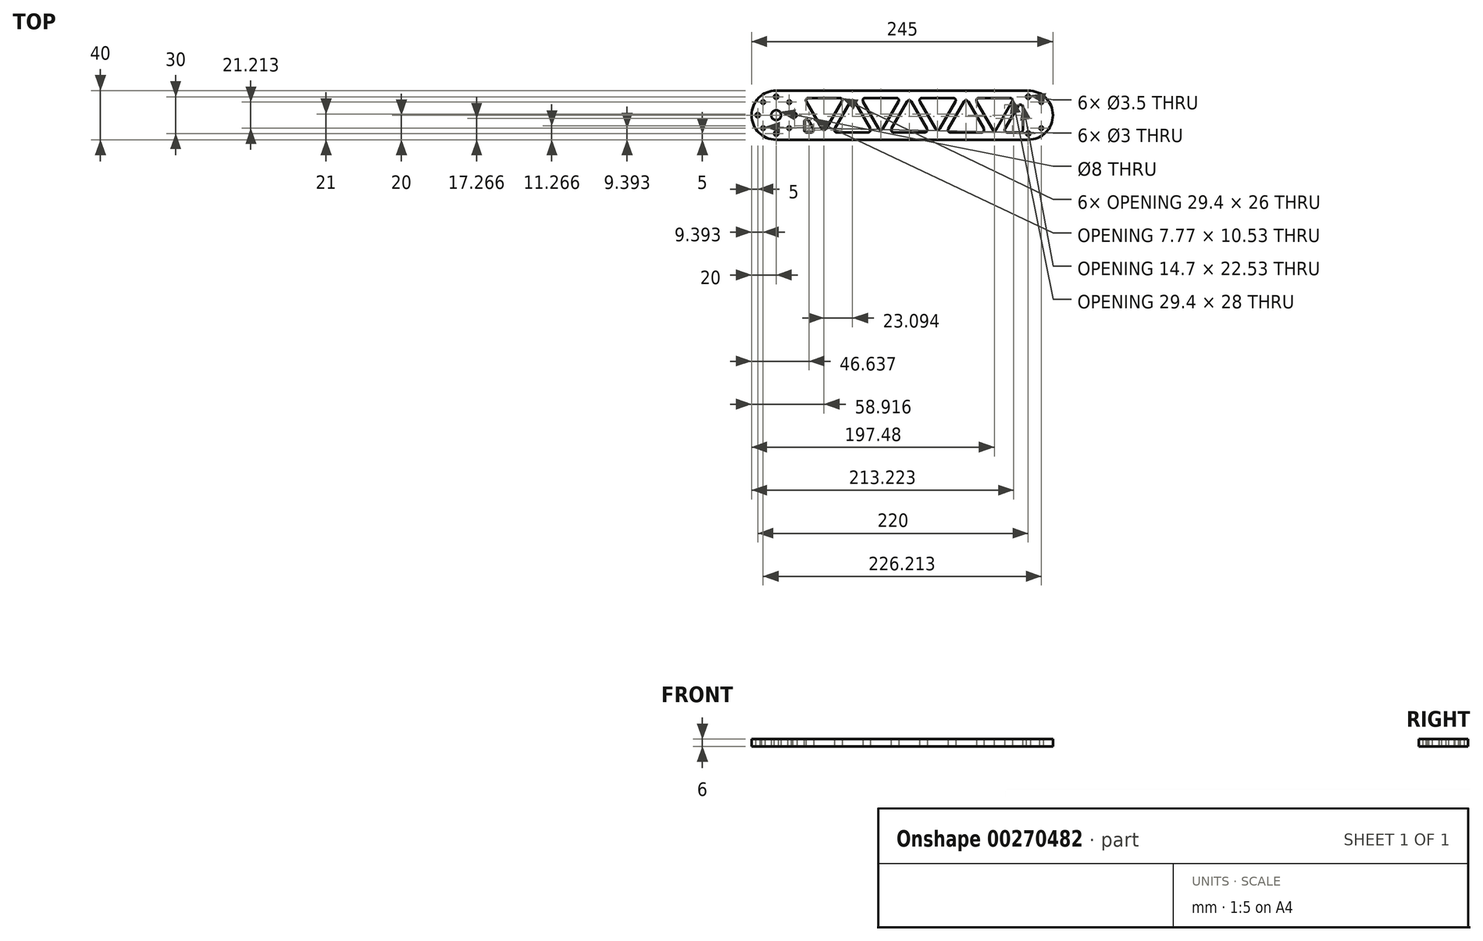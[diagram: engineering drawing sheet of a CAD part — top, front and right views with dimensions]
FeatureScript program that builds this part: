
annotation { "Feature Type Name" : "Feature", "Feature Type Description" : "" }
export const myFeature = defineFeature(function(context is Context, id is Id, definition is map)
    precondition{}
    {
        {
            var Q0;
            Q0=qCreatedBy(makeId("Top.planeOp"),FACE);
            var sketch = newSketch(context, id + "F0", { "sketchPlane" : qUnion([Q0])});
            skLineSegment(sketch, "E0.bottom", {"start": v(0, 0) * mm, "end": v(205, 0) * mm});
            skLineSegment(sketch, "E0.top", {"start": v(0, 40) * mm, "end": v(205, 40) * mm});
            skArc(sketch, "E1", {"start": v(205, 40) * mm, "mid": v(225, 20) * mm, "end": v(205, 0) * mm});
            skArc(sketch, "E2", {"start": v(0, 40) * mm, "mid": v(-20, 20) * mm, "end": v(0, 0) * mm});
            skCircle(sketch, "E3", {"center": v(0, 20) * mm, "radius": 15 * mm, "construction": true});
            skCircle(sketch, "E4", {"center": v(0, 35) * mm, "radius": 1.75 * mm});
            skCircle(sketch, "E5.1.0", {"center": v(-15, 20) * mm, "radius": 1.75 * mm});
            skCircle(sketch, "E5.2.0", {"center": v(0, 5) * mm, "radius": 1.75 * mm});
            skCircle(sketch, "E5.3.0", {"center": v(15, 20) * mm, "radius": 1.75 * mm});
            skLineSegment(sketch, "E6", {"start": v(0, 20) * mm, "end": v(10.6, 30.6) * mm});
            skCircle(sketch, "E7", {"center": v(10.6, 30.6) * mm, "radius": 1.5 * mm});
            skCircle(sketch, "E8.1.0", {"center": v(-10.6, 30.6) * mm, "radius": 1.5 * mm});
            skCircle(sketch, "E8.2.0", {"center": v(-10.6, 9.4) * mm, "radius": 1.5 * mm});
            skCircle(sketch, "E8.3.0", {"center": v(10.6, 9.4) * mm, "radius": 1.5 * mm});
            skCircle(sketch, "E9", {"center": v(0, 20) * mm, "radius": 4 * mm});
            skLineSegment(sketch, "E10", {"start": v(102.5, 40) * mm, "end": v(102.5, 0) * mm, "construction": true});
            skCircle(sketch, "E11.MirrorC", {"center": v(215.6, 30.6) * mm, "radius": 1.5 * mm});
            skCircle(sketch, "E12.MirrorC", {"center": v(215.6, 9.4) * mm, "radius": 1.5 * mm});
            skLineSegment(sketch, "E13.MirrorCS", {"start": v(205, 20) * mm, "end": v(194.4, 30.6) * mm});
            skCircle(sketch, "E14.MirrorC", {"center": v(205, 20) * mm, "radius": 15 * mm, "construction": true});
            skCircle(sketch, "E15", {"center": v(205, 5) * mm, "radius": 1.75 * mm});
            skCircle(sketch, "E16", {"center": v(205, 35) * mm, "radius": 1.75 * mm});
            skSolve(sketch);
        }
        {
            var Q0;
            Q0 = qSketchRegion(id + "F0", true);
            extrude(context, id + "F1", {"entities" : qUnion([Q0]), "depth" : 6 * mm});
        }
        {
            var Q0;
            Q0=makeQuery(id+"F1.opExtrude","CAP_FACE",FACE,{"disambiguationData":[OSD([sQuery(id+"F0.wireOp",EDGE,"E0.bottom"),sQuery(id+"F0.wireOp",EDGE,"E0.top"),sQuery(id+"F0.wireOp",EDGE,"E2"),sQuery(id+"F0.wireOp",EDGE,"E4"),sQuery(id+"F0.wireOp",EDGE,"E5.1.0"),sQuery(id+"F0.wireOp",EDGE,"E5.2.0"),sQuery(id+"F0.wireOp",EDGE,"E5.3.0"),sQuery(id+"F0.wireOp",EDGE,"E7"),sQuery(id+"F0.wireOp",EDGE,"E8.1.0"),sQuery(id+"F0.wireOp",EDGE,"E8.2.0"),sQuery(id+"F0.wireOp",EDGE,"E8.3.0"),sQuery(id+"F0.wireOp",EDGE,"E9"),sQuery(id+"F0.wireOp",EDGE,"41661442-f439-4f29-86a3-6f938a79d0c80.MirrorC"),sQuery(id+"F0.wireOp",EDGE,"E11.MirrorC"),sQuery(id+"F0.wireOp",EDGE,"E12.MirrorC"),sQuery(id+"F0.wireOp",EDGE,"E1"),sQuery(id+"F0.wireOp",EDGE,"41661442-f439-4f29-86a3-6f938a79d0c812.MirrorC")])],"isStart":false});
            var sketch = newSketch(context, id + "F2", { "sketchPlane" : qUnion([Q0])});
            skLineSegment(sketch, "E17.left", {"start": v(22.75, 34) * mm, "end": v(22.75, 6) * mm, "construction": true});
            skLineSegment(sketch, "E17.right", {"start": v(200.57, 33.96) * mm, "end": v(200.57, 6) * mm, "construction": true});
            skLineSegment(sketch, "E18", {"start": v(22.75, 34) * mm, "end": v(55.08, 34) * mm});
            skLineSegment(sketch, "E19", {"start": v(55.08, 34) * mm, "end": v(38.92, 6) * mm});
            skLineSegment(sketch, "E20", {"start": v(38.92, 6) * mm, "end": v(22.75, 34) * mm});
            skLineSegment(sketch, "E21", {"start": v(45.84, 6) * mm, "end": v(62, 34) * mm});
            skLineSegment(sketch, "E22", {"start": v(62, 34) * mm, "end": v(78.18, 6) * mm});
            skLineSegment(sketch, "E23", {"start": v(78.18, 6) * mm, "end": v(45.84, 6) * mm});
            skLineSegment(sketch, "E24", {"start": v(22.75, 6) * mm, "end": v(200.57, 6) * mm, "construction": true});
            skLineSegment(sketch, "E25", {"start": v(55.08, 34) * mm, "end": v(22.75, 34) * mm, "construction": true});
            skPoint(sketch, "E26.visualSharp", {"position": v(22.75, 34) * mm});
            skPoint(sketch, "E27.visualSharp", {"position": v(38.92, 6) * mm});
            skLineSegment(sketch, "E28.1.0.0", {"start": v(101.27, 34) * mm, "end": v(85.1, 6) * mm});
            skPoint(sketch, "E28.1.0.1", {"position": v(68.94, 34) * mm});
            skLineSegment(sketch, "E28.1.0.2", {"start": v(85.1, 6) * mm, "end": v(68.94, 34) * mm});
            skLineSegment(sketch, "E28.1.0.3", {"start": v(108.2, 34) * mm, "end": v(124.36, 6) * mm});
            skLineSegment(sketch, "E28.1.0.4", {"start": v(92.03, 6) * mm, "end": v(108.2, 34) * mm});
            skPoint(sketch, "E28.1.0.5", {"position": v(85.1, 6) * mm});
            skLineSegment(sketch, "E28.1.0.6", {"start": v(101.27, 34) * mm, "end": v(68.94, 34) * mm, "construction": true});
            skLineSegment(sketch, "E28.1.0.7", {"start": v(124.36, 6) * mm, "end": v(92.03, 6) * mm});
            skLineSegment(sketch, "E28.1.0.8", {"start": v(68.94, 34) * mm, "end": v(101.27, 34) * mm});
            skLineSegment(sketch, "E28.2.0.0", {"start": v(147.46, 34) * mm, "end": v(131.3, 6) * mm});
            skPoint(sketch, "E28.2.0.1", {"position": v(115.13, 34) * mm});
            skLineSegment(sketch, "E28.2.0.2", {"start": v(131.3, 6) * mm, "end": v(115.13, 34) * mm});
            skLineSegment(sketch, "E28.2.0.3", {"start": v(154.39, 34) * mm, "end": v(170.55, 6) * mm});
            skLineSegment(sketch, "E28.2.0.4", {"start": v(138.22, 6) * mm, "end": v(154.39, 34) * mm});
            skPoint(sketch, "E28.2.0.5", {"position": v(131.3, 6) * mm});
            skLineSegment(sketch, "E28.2.0.6", {"start": v(147.46, 34) * mm, "end": v(115.13, 34) * mm, "construction": true});
            skLineSegment(sketch, "E28.2.0.7", {"start": v(170.55, 6) * mm, "end": v(138.22, 6) * mm});
            skLineSegment(sketch, "E28.2.0.8", {"start": v(115.13, 34) * mm, "end": v(147.46, 34) * mm});
            skLineSegment(sketch, "E28.direction1", {"start": v(38.92, 6) * mm, "end": v(85.1, 6) * mm, "construction": true});
            skLineSegment(sketch, "E29.0.3.0", {"start": v(193.65, 34) * mm, "end": v(177.48, 6) * mm});
            skPoint(sketch, "E29.3.3.0", {"position": v(161.31, 34) * mm});
            skLineSegment(sketch, "E29.4.3.0", {"start": v(177.48, 6) * mm, "end": v(161.31, 34) * mm});
            skPoint(sketch, "E29.13.3.0", {"position": v(177.48, 6) * mm});
            skLineSegment(sketch, "E29.14.3.0", {"start": v(193.65, 34) * mm, "end": v(161.31, 34) * mm, "construction": true});
            skLineSegment(sketch, "E29.20.3.0", {"start": v(161.31, 34) * mm, "end": v(193.65, 34) * mm});
            skLineSegment(sketch, "E30", {"start": v(200.57, 34) * mm, "end": v(184.4, 6) * mm});
            skLineSegment(sketch, "E31", {"start": v(184.4, 6) * mm, "end": v(200.57, 6) * mm});
            skLineSegment(sketch, "E32", {"start": v(200.57, 6) * mm, "end": v(200.57, 34) * mm});
            skLineSegment(sketch, "E33", {"start": v(22.75, 6) * mm, "end": v(31.99, 6) * mm});
            skLineSegment(sketch, "E34", {"start": v(31.99, 6) * mm, "end": v(22.75, 22) * mm});
            skLineSegment(sketch, "E35", {"start": v(22.75, 22) * mm, "end": v(22.75, 6) * mm});
            skSolve(sketch);
        }
        {
            var Q0;
            Q0 = qSketchRegion(id + "F2", true);
            extrude(context, id + "F3", {"entities" : qUnion([Q0]), "operationType" : NewBodyOperationType.REMOVE, "endBound" : BoundingType.THROUGH_ALL, "oppositeDirection" : true, "depth" : 25 * mm});
        }
        {
            var Q0;
            Q0=makeQuery(id+"F3.boolean.opBoolean","COPY",EDGE,{"derivedFrom":makeQuery(id+"F3.opExtrude","SWEPT_EDGE",EDGE,{"disambiguationData":[OSD([sQuery(id+"F2.wireOp",EDGE,"E18"),sQuery(id+"F2.wireOp",EDGE,"E20")])]})});
            var Q1;
            Q1=makeQuery(id+"F3.boolean.opBoolean","COPY",EDGE,{"derivedFrom":makeQuery(id+"F3.opExtrude","SWEPT_EDGE",EDGE,{"disambiguationData":[OSD([sQuery(id+"F2.wireOp",EDGE,"E18"),sQuery(id+"F2.wireOp",EDGE,"E19")])]})});
            var Q2;
            Q2=makeQuery(id+"F3.boolean.opBoolean","COPY",EDGE,{"derivedFrom":makeQuery(id+"F3.opExtrude","SWEPT_EDGE",EDGE,{"disambiguationData":[OSD([sQuery(id+"F2.wireOp",EDGE,"E19"),sQuery(id+"F2.wireOp",EDGE,"E20")])]})});
            var Q3;
            Q3=makeQuery(id+"F3.boolean.opBoolean","COPY",EDGE,{"derivedFrom":makeQuery(id+"F3.opExtrude","SWEPT_EDGE",EDGE,{"disambiguationData":[OSD([sQuery(id+"F2.wireOp",EDGE,"E21"),sQuery(id+"F2.wireOp",EDGE,"E23")])]})});
            var Q4;
            Q4=makeQuery(id+"F3.boolean.opBoolean","COPY",EDGE,{"derivedFrom":makeQuery(id+"F3.opExtrude","SWEPT_EDGE",EDGE,{"disambiguationData":[OSD([sQuery(id+"F2.wireOp",EDGE,"E21"),sQuery(id+"F2.wireOp",EDGE,"E22")])]})});
            var Q5;
            Q5=makeQuery(id+"F3.boolean.opBoolean","COPY",EDGE,{"derivedFrom":makeQuery(id+"F3.opExtrude","SWEPT_EDGE",EDGE,{"disambiguationData":[OSD([sQuery(id+"F2.wireOp",EDGE,"E22"),sQuery(id+"F2.wireOp",EDGE,"E23")])]})});
            var Q6;
            Q6=makeQuery(id+"F3.boolean.opBoolean","COPY",EDGE,{"derivedFrom":makeQuery(id+"F3.opExtrude","SWEPT_EDGE",EDGE,{"disambiguationData":[OSD([sQuery(id+"F2.wireOp",EDGE,"E34"),sQuery(id+"F2.wireOp",EDGE,"E35")])]})});
            var Q7;
            Q7=makeQuery(id+"F3.boolean.opBoolean","COPY",EDGE,{"derivedFrom":makeQuery(id+"F3.opExtrude","SWEPT_EDGE",EDGE,{"disambiguationData":[OSD([sQuery(id+"F2.wireOp",EDGE,"E33"),sQuery(id+"F2.wireOp",EDGE,"E35")])]})});
            var Q8;
            Q8=makeQuery(id+"F3.boolean.opBoolean","COPY",EDGE,{"derivedFrom":makeQuery(id+"F3.opExtrude","SWEPT_EDGE",EDGE,{"disambiguationData":[OSD([sQuery(id+"F2.wireOp",EDGE,"E33"),sQuery(id+"F2.wireOp",EDGE,"E34")])]})});
            var Q9;
            Q9=makeQuery(id+"F3.boolean.opBoolean","COPY",EDGE,{"derivedFrom":makeQuery(id+"F3.opExtrude","SWEPT_EDGE",EDGE,{"disambiguationData":[OSD([sQuery(id+"F2.wireOp",EDGE,"E28.1.0.2"),sQuery(id+"F2.wireOp",EDGE,"E28.1.0.8")])]})});
            var Q10;
            Q10=makeQuery(id+"F3.boolean.opBoolean","COPY",EDGE,{"derivedFrom":makeQuery(id+"F3.opExtrude","SWEPT_EDGE",EDGE,{"disambiguationData":[OSD([sQuery(id+"F2.wireOp",EDGE,"E28.1.0.0"),sQuery(id+"F2.wireOp",EDGE,"E28.1.0.8")])]})});
            var Q11;
            Q11=makeQuery(id+"F3.boolean.opBoolean","COPY",EDGE,{"derivedFrom":makeQuery(id+"F3.opExtrude","SWEPT_EDGE",EDGE,{"disambiguationData":[OSD([sQuery(id+"F2.wireOp",EDGE,"E28.1.0.0"),sQuery(id+"F2.wireOp",EDGE,"E28.1.0.2")])]})});
            var Q12;
            Q12=makeQuery(id+"F3.boolean.opBoolean","COPY",EDGE,{"derivedFrom":makeQuery(id+"F3.opExtrude","SWEPT_EDGE",EDGE,{"disambiguationData":[OSD([sQuery(id+"F2.wireOp",EDGE,"E28.1.0.4"),sQuery(id+"F2.wireOp",EDGE,"E28.1.0.7")])]})});
            var Q13;
            Q13=makeQuery(id+"F3.boolean.opBoolean","COPY",EDGE,{"derivedFrom":makeQuery(id+"F3.opExtrude","SWEPT_EDGE",EDGE,{"disambiguationData":[OSD([sQuery(id+"F2.wireOp",EDGE,"E28.1.0.3"),sQuery(id+"F2.wireOp",EDGE,"E28.1.0.4")])]})});
            var Q14;
            Q14=makeQuery(id+"F3.boolean.opBoolean","COPY",EDGE,{"derivedFrom":makeQuery(id+"F3.opExtrude","SWEPT_EDGE",EDGE,{"disambiguationData":[OSD([sQuery(id+"F2.wireOp",EDGE,"E28.1.0.3"),sQuery(id+"F2.wireOp",EDGE,"E28.1.0.7")])]})});
            var Q15;
            Q15=makeQuery(id+"F3.boolean.opBoolean","COPY",EDGE,{"derivedFrom":makeQuery(id+"F3.opExtrude","SWEPT_EDGE",EDGE,{"disambiguationData":[OSD([sQuery(id+"F2.wireOp",EDGE,"E28.2.0.2"),sQuery(id+"F2.wireOp",EDGE,"E28.2.0.8")])]})});
            var Q16;
            Q16=makeQuery(id+"F3.boolean.opBoolean","COPY",EDGE,{"derivedFrom":makeQuery(id+"F3.opExtrude","SWEPT_EDGE",EDGE,{"disambiguationData":[OSD([sQuery(id+"F2.wireOp",EDGE,"E29.4.3.0"),sQuery(id+"F2.wireOp",EDGE,"E29.20.3.0")])]})});
            var Q17;
            Q17=makeQuery(id+"F3.boolean.opBoolean","COPY",EDGE,{"derivedFrom":makeQuery(id+"F3.opExtrude","SWEPT_EDGE",EDGE,{"disambiguationData":[OSD([sQuery(id+"F2.wireOp",EDGE,"E28.2.0.0"),sQuery(id+"F2.wireOp",EDGE,"E28.2.0.8")])]})});
            var Q18;
            Q18=makeQuery(id+"F3.boolean.opBoolean","COPY",EDGE,{"derivedFrom":makeQuery(id+"F3.opExtrude","SWEPT_EDGE",EDGE,{"disambiguationData":[OSD([sQuery(id+"F2.wireOp",EDGE,"E29.0.3.0"),sQuery(id+"F2.wireOp",EDGE,"E29.20.3.0")])]})});
            var Q19;
            Q19=makeQuery(id+"F3.boolean.opBoolean","COPY",EDGE,{"derivedFrom":makeQuery(id+"F3.opExtrude","SWEPT_EDGE",EDGE,{"disambiguationData":[OSD([sQuery(id+"F2.wireOp",EDGE,"E28.2.0.0"),sQuery(id+"F2.wireOp",EDGE,"E28.2.0.2")])]})});
            var Q20;
            Q20=makeQuery(id+"F3.boolean.opBoolean","COPY",EDGE,{"derivedFrom":makeQuery(id+"F3.opExtrude","SWEPT_EDGE",EDGE,{"disambiguationData":[OSD([sQuery(id+"F2.wireOp",EDGE,"E28.2.0.3"),sQuery(id+"F2.wireOp",EDGE,"E28.2.0.4")])]})});
            var Q21;
            Q21=makeQuery(id+"F3.boolean.opBoolean","COPY",EDGE,{"derivedFrom":makeQuery(id+"F3.opExtrude","SWEPT_EDGE",EDGE,{"disambiguationData":[OSD([sQuery(id+"F2.wireOp",EDGE,"E28.2.0.3"),sQuery(id+"F2.wireOp",EDGE,"E28.2.0.7")])]})});
            var Q22;
            Q22=makeQuery(id+"F3.boolean.opBoolean","COPY",EDGE,{"derivedFrom":makeQuery(id+"F3.opExtrude","SWEPT_EDGE",EDGE,{"disambiguationData":[OSD([sQuery(id+"F2.wireOp",EDGE,"E28.2.0.4"),sQuery(id+"F2.wireOp",EDGE,"E28.2.0.7")])]})});
            var Q23;
            Q23=makeQuery(id+"F3.boolean.opBoolean","COPY",EDGE,{"derivedFrom":makeQuery(id+"F3.opExtrude","SWEPT_EDGE",EDGE,{"disambiguationData":[OSD([sQuery(id+"F2.wireOp",EDGE,"E31"),sQuery(id+"F2.wireOp",EDGE,"E32")])]})});
            var Q24;
            Q24=makeQuery(id+"F3.boolean.opBoolean","COPY",EDGE,{"derivedFrom":makeQuery(id+"F3.opExtrude","SWEPT_EDGE",EDGE,{"disambiguationData":[OSD([sQuery(id+"F2.wireOp",EDGE,"E30"),sQuery(id+"F2.wireOp",EDGE,"E31")])]})});
            var Q25;
            Q25=makeQuery(id+"F3.boolean.opBoolean","COPY",EDGE,{"derivedFrom":makeQuery(id+"F3.opExtrude","SWEPT_EDGE",EDGE,{"disambiguationData":[OSD([sQuery(id+"F2.wireOp",EDGE,"E30"),sQuery(id+"F2.wireOp",EDGE,"E32")])]})});
            fillet(context, id + "F4", {"entities" : qUnion([Q0, Q1, Q2, Q3, Q4, Q5, Q6, Q7, Q8, Q9, Q10, Q11, Q12, Q13, Q14, Q15, Q16, Q17, Q18, Q19, Q20, Q21, Q22, Q23, Q24, Q25]), "radius" : 2 * mm, "tangentPropagation" : true, "allowEdgeOverflow" : false});
        }
    });
